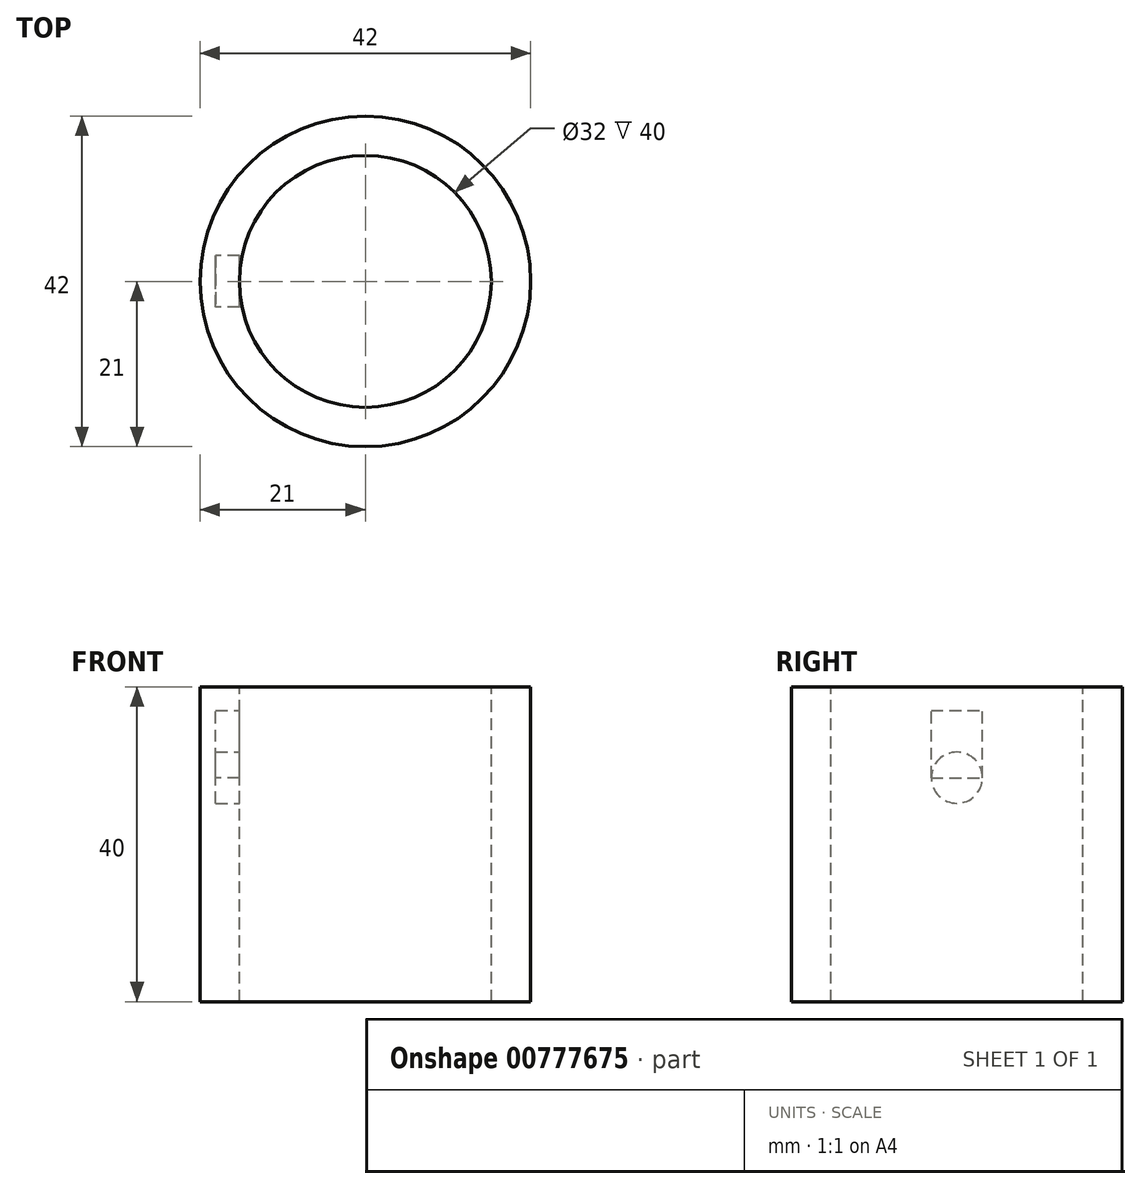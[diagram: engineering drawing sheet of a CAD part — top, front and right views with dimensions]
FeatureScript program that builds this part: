
annotation { "Feature Type Name" : "Feature", "Feature Type Description" : "" }
export const myFeature = defineFeature(function(context is Context, id is Id, definition is map)
    precondition{}
    {
        {
            var Q0;
            Q0=qCreatedBy(makeId("Top.planeOp"),FACE);
            var sketch = newSketch(context, id + "F0", { "sketchPlane" : qUnion([Q0])});
            skCircle(sketch, "E0", {"center": v(0, 0) * mm, "radius": 16 * mm});
            skCircle(sketch, "E1.0", {"center": v(0, 0) * mm, "radius": 21 * mm});
            skSolve(sketch);
        }
        {
            var Q0;
            Q0=makeQuery(id+"F0.imprint","IMPRINT",FACE,{"disambiguationData":[TD([[makeQuery(id+"F0.imprint","IMPRINT",EDGE,{"derivedFrom":sQuery(id+"F0.wireOp",EDGE,"E0")}),-1.0]])]});
            extrude(context, id + "F1", {"entities" : qUnion([Q0]), "oppositeDirection" : true, "depth" : 40 * mm, "offsetDistance" : 25 * mm});
        }
        {
            var Q0;
            Q0=qCreatedBy(makeId("Front.planeOp"),FACE);
            var sketch = newSketch(context, id + "F2", { "sketchPlane" : qUnion([Q0])});
            skLineSegment(sketch, "E2", {"start": v(-19, -40) * mm, "end": v(-19, -3) * mm});
            skLineSegment(sketch, "E3", {"start": v(-19, -3) * mm, "end": v(-16, -3) * mm});
            skLineSegment(sketch, "E4", {"start": v(-16, -14.8) * mm, "end": v(-21, -14.8) * mm});
            skLineSegment(sketch, "E5", {"start": v(-16, -8.3) * mm, "end": v(-21, -8.3) * mm});
            skLineSegment(sketch, "E6", {"start": v(-16, -11.55) * mm, "end": v(-19, -11.55) * mm});
            skLineSegment(sketch, "E7", {"start": v(-16, -14.8) * mm, "end": v(-16, -8.3) * mm});
            skLineSegment(sketch, "E8", {"start": v(-16, -8.3) * mm, "end": v(-16, -3) * mm});
            skLineSegment(sketch, "E9", {"start": v(-16, 0) * mm, "end": v(-16, -40) * mm});
            skLineSegment(sketch, "E10", {"start": v(16, -40) * mm, "end": v(16, 0) * mm});
            skLineSegment(sketch, "E11", {"start": v(-21, 0) * mm, "end": v(-21, -40) * mm});
            skLineSegment(sketch, "E12", {"start": v(21, -40) * mm, "end": v(21, 0) * mm});
            skLineSegment(sketch, "E13", {"start": v(-19, -3) * mm, "end": v(-21, -3) * mm});
            skSolve(sketch);
        }
        {
            var Q0;
            {var subQ0=sQuery(id+"F2.wireOp",EDGE,"E6");Q0=makeQuery(id+"F2.imprint","IMPRINT",FACE,{"disambiguationData":[TD([[makeQuery(id+"F2.imprint","IMPRINT",EDGE,{"derivedFrom":subQ0}),1.0]])]});}
            var Q1;
            Q1=sQuery(id+"F2.wireOp",EDGE,"E6");
            revolve(context, id + "F3", {"surfaceOperationType" : NewSurfaceOperationType.NEW, "entities" : qUnion([Q0]), "axis" : qUnion([Q1]), "revolveType" : RevolveType.FULL});
        }
        {
            var Q0;
            {var subQ0=sQuery(id+"F2.wireOp",EDGE,"E3");Q0=makeQuery(id+"F2.imprint","IMPRINT",FACE,{"disambiguationData":[TD([[makeQuery(id+"F2.imprint","IMPRINT",EDGE,{"derivedFrom":subQ0}),-1.0]])]});}
            var Q1;
            {var subQ0=sQuery(id+"F2.wireOp",EDGE,"E6");Q1=makeQuery(id+"F2.imprint","IMPRINT",FACE,{"disambiguationData":[TD([[makeQuery(id+"F2.imprint","IMPRINT",EDGE,{"derivedFrom":subQ0}),-1.0]])]});}
            var Q2;
            Q2=makeQuery(id+"F3.opRevolve","SWEPT_FACE",FACE,{"disambiguationData":[OSD([sQuery(id+"F2.wireOp",EDGE,"E4")])]});
            extrude(context, id + "F4", {"entities" : qUnion([Q0, Q1]), "depth" : 6.5 * mm, "endBoundEntityFace" : qUnion([Q2]), "offsetDistance" : 25 * mm, "symmetric" : true});
        }
    });
